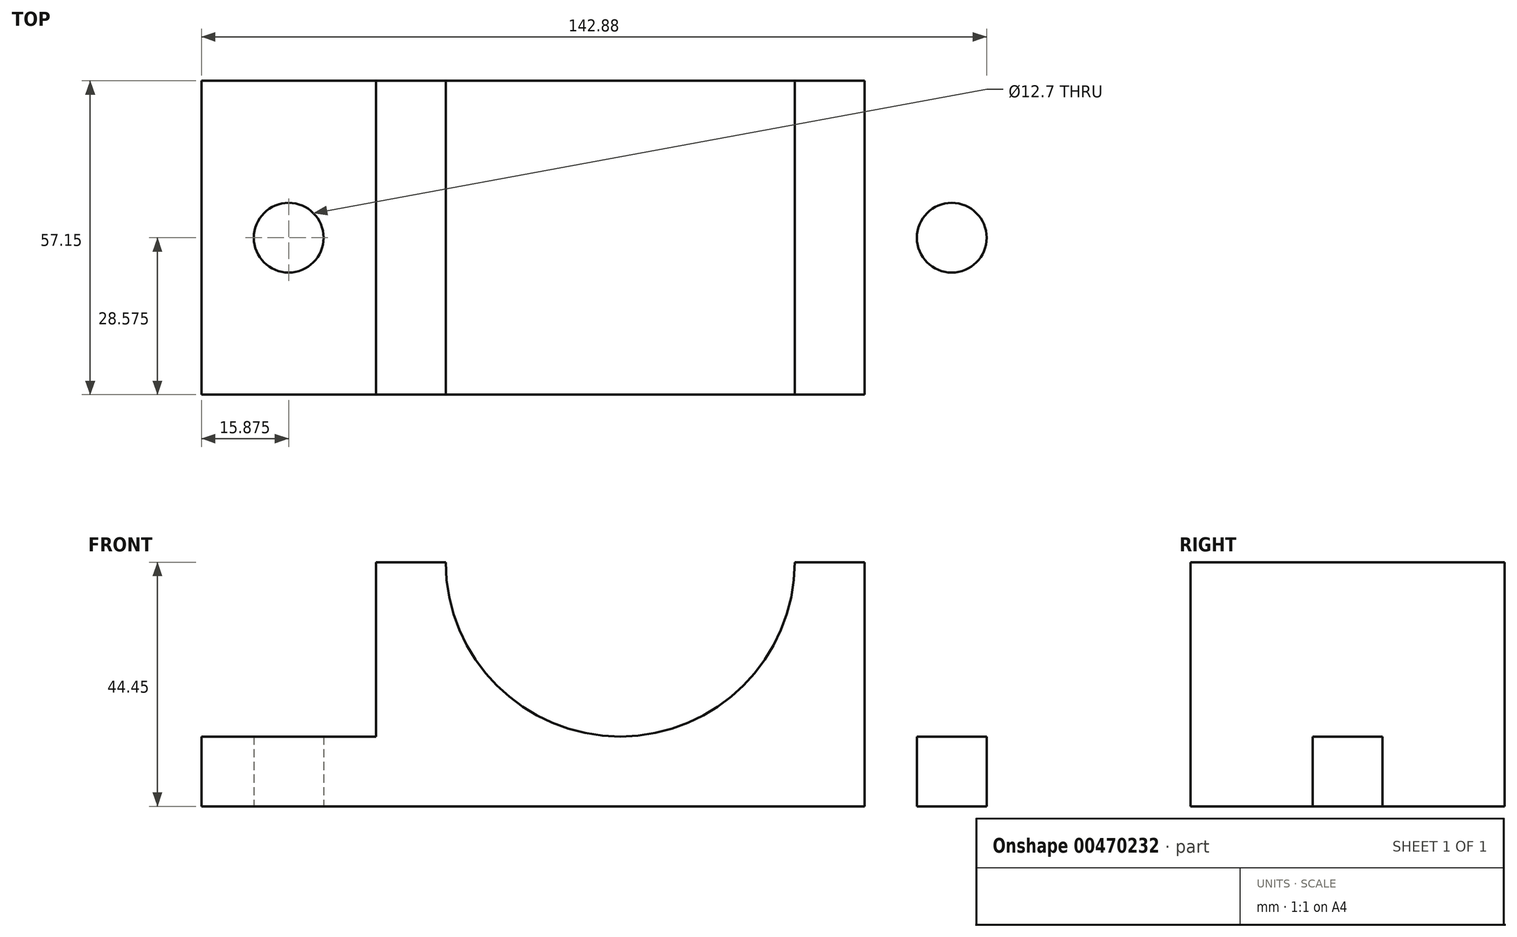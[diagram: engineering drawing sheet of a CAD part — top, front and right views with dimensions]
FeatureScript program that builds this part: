
annotation { "Feature Type Name" : "Feature", "Feature Type Description" : "" }
export const myFeature = defineFeature(function(context is Context, id is Id, definition is map)
    precondition{}
    {
        {
            var Q0;
            Q0=qCreatedBy(makeId("Front.planeOp"),FACE);
            var sketch = newSketch(context, id + "F0", { "sketchPlane" : qUnion([Q0])});
            skLineSegment(sketch, "E0", {"start": v(-39.63, 0) * mm, "end": v(112.77, 0) * mm});
            skLineSegment(sketch, "E1", {"start": v(-39.63, 0) * mm, "end": v(-39.63, 12.7) * mm});
            skLineSegment(sketch, "E2", {"start": v(-39.63, 12.7) * mm, "end": v(112.77, 12.7) * mm});
            skLineSegment(sketch, "E3", {"start": v(112.77, 12.7) * mm, "end": v(112.77, 0) * mm});
            skLineSegment(sketch, "E4", {"start": v(-7.88, 12.7) * mm, "end": v(-7.88, 44.45) * mm});
            skLineSegment(sketch, "E5", {"start": v(-7.88, 44.45) * mm, "end": v(81.02, 44.45) * mm});
            skLineSegment(sketch, "E6", {"start": v(81.02, 44.45) * mm, "end": v(81.02, 12.7) * mm});
            skArc(sketch, "E7", {"start": v(36.57, 12.7) * mm, "mid": v(59.02, 22) * mm, "end": v(68.32, 44.45) * mm});
            skArc(sketch, "E8", {"start": v(36.57, 12.7) * mm, "mid": v(14.12, 22) * mm, "end": v(4.82, 44.45) * mm});
            skSolve(sketch);
        }
        {
            var Q0;
            {var subQ0=sQuery(id+"F0.wireOp",EDGE,"E4");Q0=makeQuery(id+"F0.imprint","IMPRINT",FACE,{"disambiguationData":[TD([[makeQuery(id+"F0.imprint","IMPRINT",EDGE,{"derivedFrom":subQ0}),-1.0]])]});}
            var Q1;
            Q1=makeQuery(id+"F0.imprint","IMPRINT",FACE,{"disambiguationData":[TD([[makeQuery(id+"F0.imprint","IMPRINT",EDGE,{"derivedFrom":sQuery(id+"F0.wireOp",EDGE,"E0")}),1.0]])]});
            var Q2;
            {var subQ0=sQuery(id+"F0.wireOp",EDGE,"E6");Q2=makeQuery(id+"F0.imprint","IMPRINT",FACE,{"disambiguationData":[TD([[makeQuery(id+"F0.imprint","IMPRINT",EDGE,{"derivedFrom":subQ0}),-1.0]])]});}
            extrude(context, id + "F1", {"entities" : qUnion([Q0, Q1, Q2]), "depth" : 57.15 * mm});
        }
        {
            var Q0;
            Q0=qCreatedBy(makeId("Top.planeOp"),FACE);
            var sketch = newSketch(context, id + "F2", { "sketchPlane" : qUnion([Q0])});
            skLineSegment(sketch, "E9.0.0", {"start": v(-7.88, 0) * mm, "end": v(-39.63, 0) * mm});
            skLineSegment(sketch, "E9.0.1", {"start": v(-39.63, 0) * mm, "end": v(-39.63, -57.15) * mm});
            skLineSegment(sketch, "E9.0.2", {"start": v(-39.63, -57.15) * mm, "end": v(-7.88, -57.15) * mm});
            skLineSegment(sketch, "E9.0.3", {"start": v(-7.88, -57.15) * mm, "end": v(-7.88, 0) * mm});
            skCircle(sketch, "E10", {"center": v(-23.75, -28.58) * mm, "radius": 6.35 * mm});
            skPoint(sketch, "E10.centerSnap0", {"position": v(-39.63, -28.58) * mm});
            skPoint(sketch, "E10.centerSnap1", {"position": v(-23.75, 0) * mm});
            skLineSegment(sketch, "E11.0.0", {"start": v(4.82, 0) * mm, "end": v(-7.88, 0) * mm});
            skLineSegment(sketch, "E11.0.1", {"start": v(-7.88, 0) * mm, "end": v(-7.88, -57.15) * mm});
            skLineSegment(sketch, "E11.0.2", {"start": v(-7.88, -57.15) * mm, "end": v(4.82, -57.15) * mm});
            skLineSegment(sketch, "E11.0.3", {"start": v(4.82, -57.15) * mm, "end": v(4.82, 0) * mm});
            skLineSegment(sketch, "E11.1.0", {"start": v(4.82, 0) * mm, "end": v(68.32, 0) * mm});
            skLineSegment(sketch, "E11.1.1", {"start": v(4.82, 0) * mm, "end": v(4.82, -57.15) * mm});
            skLineSegment(sketch, "E11.1.2", {"start": v(68.32, -57.15) * mm, "end": v(4.82, -57.15) * mm});
            skLineSegment(sketch, "E11.1.3", {"start": v(68.32, -57.15) * mm, "end": v(68.32, 0) * mm});
            skLineSegment(sketch, "E11.2.0", {"start": v(81.02, 0) * mm, "end": v(68.32, 0) * mm});
            skLineSegment(sketch, "E11.2.1", {"start": v(68.32, 0) * mm, "end": v(68.32, -57.15) * mm});
            skLineSegment(sketch, "E11.2.2", {"start": v(68.32, -57.15) * mm, "end": v(81.02, -57.15) * mm});
            skLineSegment(sketch, "E11.2.3", {"start": v(81.02, -57.15) * mm, "end": v(81.02, 0) * mm});
            skLineSegment(sketch, "E11.3.0", {"start": v(112.77, 0) * mm, "end": v(81.02, 0) * mm});
            skLineSegment(sketch, "E11.3.1", {"start": v(81.02, 0) * mm, "end": v(81.02, -57.15) * mm});
            skLineSegment(sketch, "E11.3.2", {"start": v(81.02, -57.15) * mm, "end": v(112.77, -57.15) * mm});
            skLineSegment(sketch, "E11.3.3", {"start": v(112.77, -57.15) * mm, "end": v(112.77, 0) * mm});
            skCircle(sketch, "E12.MirrorC", {"center": v(96.9, -28.58) * mm, "radius": 6.35 * mm});
            skSolve(sketch);
        }
        {
            var Q0;
            Q0=makeQuery(id+"F2.imprint","IMPRINT",FACE,{"disambiguationData":[TD([[makeQuery(id+"F2.imprint","IMPRINT",EDGE,{"derivedFrom":sQuery(id+"F2.wireOp",EDGE,"E10")}),1.0]])]});
            var Q1;
            Q1=makeQuery(id+"F2.imprint","IMPRINT",FACE,{"disambiguationData":[TD([[makeQuery(id+"F2.imprint","IMPRINT",EDGE,{"derivedFrom":sQuery(id+"F2.wireOp",EDGE,"E12.MirrorC")}),-1.0]])]});
            extrude(context, id + "F3", {"entities" : qUnion([Q0, Q1]), "operationType" : NewBodyOperationType.REMOVE, "depth" : 25.4 * mm});
        }
    });
